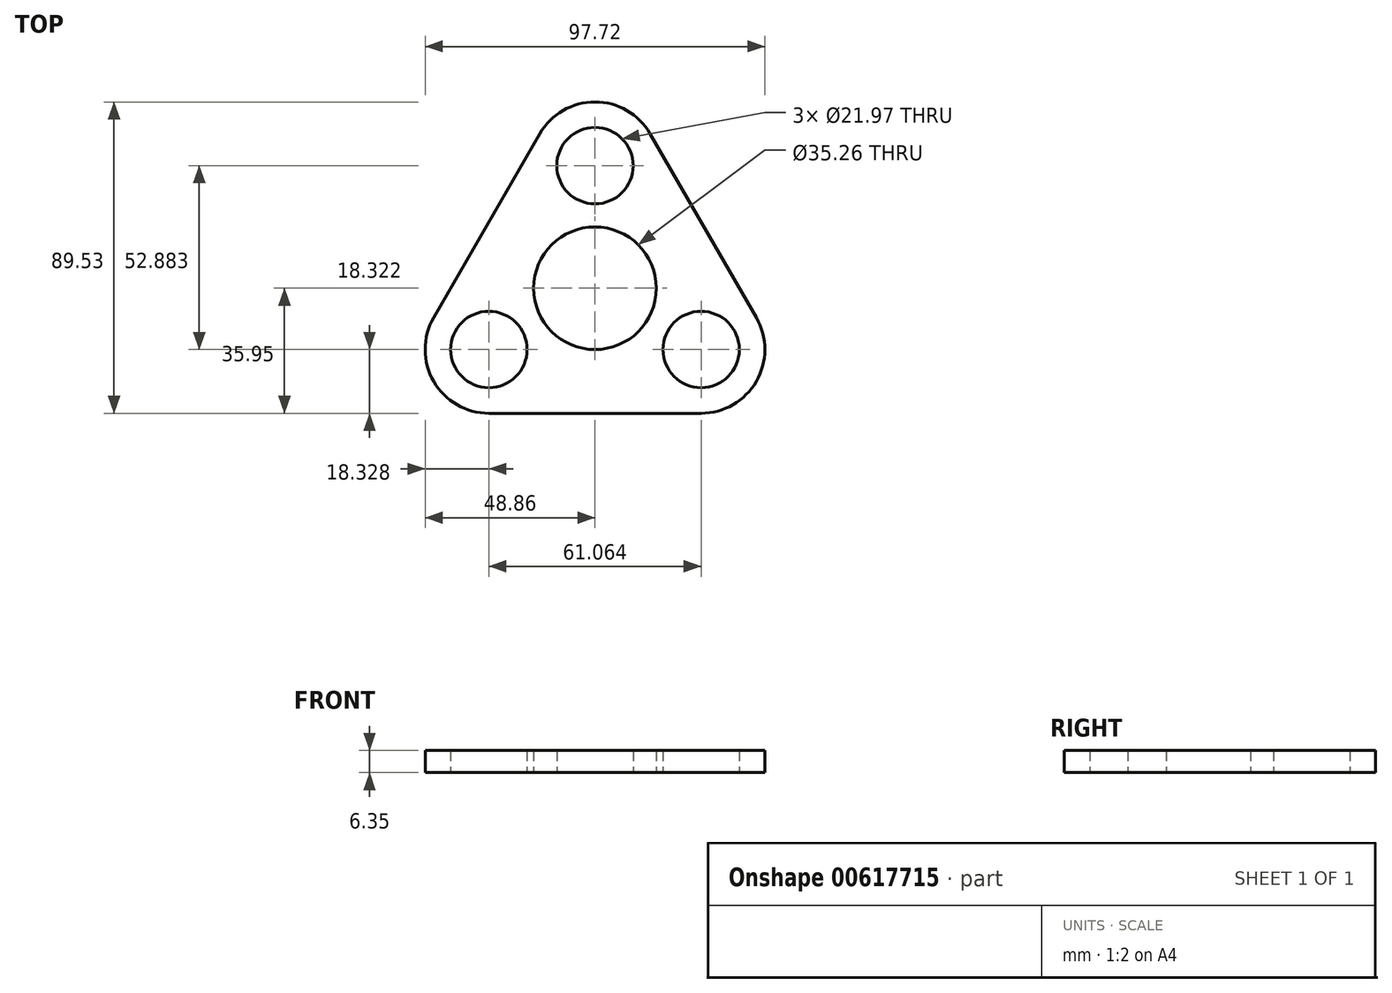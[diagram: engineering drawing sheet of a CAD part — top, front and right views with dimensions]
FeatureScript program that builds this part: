
annotation { "Feature Type Name" : "Feature", "Feature Type Description" : "" }
export const myFeature = defineFeature(function(context is Context, id is Id, definition is map)
    precondition{}
    {
        {
            var Q0;
            Q0=qCreatedBy(makeId("Top.planeOp"),FACE);
            var sketch = newSketch(context, id + "F0", { "sketchPlane" : qUnion([Q0])});
            skCircle(sketch, "E0", {"center": v(0, 0) * mm, "radius": 10.99 * mm});
            skLineSegment(sketch, "E1", {"start": v(0, 0) * mm, "end": v(0, 35.26) * mm});
            skLineSegment(sketch, "E2", {"start": v(0, 0) * mm, "end": v(30.53, -17.63) * mm});
            skLineSegment(sketch, "E3", {"start": v(0, 0) * mm, "end": v(-30.53, -17.63) * mm});
            skCircle(sketch, "E4", {"center": v(0, 35.26) * mm, "radius": 10.99 * mm});
            skCircle(sketch, "E5", {"center": v(-30.53, -17.63) * mm, "radius": 10.99 * mm});
            skCircle(sketch, "E6", {"center": v(30.53, -17.63) * mm, "radius": 10.99 * mm});
            skCircle(sketch, "E7", {"center": v(0, 0) * mm, "radius": 17.63 * mm});
            skCircle(sketch, "E8", {"center": v(-30.53, -17.63) * mm, "radius": 18.33 * mm});
            skCircle(sketch, "E9", {"center": v(0, 35.26) * mm, "radius": 18.33 * mm});
            skCircle(sketch, "E10", {"center": v(30.53, -17.63) * mm, "radius": 18.33 * mm});
            skLineSegment(sketch, "E11", {"start": v(15.87, 44.42) * mm, "end": v(46.4, -8.46) * mm});
            skLineSegment(sketch, "E12", {"start": v(-15.87, 44.42) * mm, "end": v(-46.4, -8.46) * mm});
            skLineSegment(sketch, "E13", {"start": v(-30.53, -35.95) * mm, "end": v(30.53, -35.95) * mm});
            skCircle(sketch, "E14", {"center": v(-21.16, 23.01) * mm, "radius": 6.12 * mm});
            skCircle(sketch, "E15", {"center": v(21.16, 23.01) * mm, "radius": 6.12 * mm});
            skCircle(sketch, "E16", {"center": v(0, -29.83) * mm, "radius": 6.12 * mm});
            skSolve(sketch);
        }
        {
            var Q0;
            {var subQ0=sQuery(id+"F0.wireOp",EDGE,"E12");var subQ1=sQuery(id+"F0.wireOp",EDGE,"E9");var subQ2=makeQuery(id+"F0.imprint","INTERSECT",VERTEX,{"derivedFrom":[subQ1,subQ0]});Q0=makeQuery(id+"F0.imprint","IMPRINT",FACE,{"disambiguationData":[TD([[makeQuery(id+"F0.imprint","IMPRINT",EDGE,{"disambiguationData":[TD([[subQ2,-1.0]])],"derivedFrom":subQ1}),-1.0]])]});}
            var Q1;
            {var subQ0=sQuery(id+"F0.wireOp",EDGE,"E11");var subQ1=sQuery(id+"F0.wireOp",EDGE,"E9");var subQ2=makeQuery(id+"F0.imprint","INTERSECT",VERTEX,{"derivedFrom":[subQ1,subQ0]});Q1=makeQuery(id+"F0.imprint","IMPRINT",FACE,{"disambiguationData":[TD([[makeQuery(id+"F0.imprint","IMPRINT",EDGE,{"disambiguationData":[TD([[subQ2,1.0]])],"derivedFrom":subQ1}),-1.0]])]});}
            var Q2;
            Q2 = qSketchRegion(id + "F0", true);
            extrude(context, id + "F1", {"entities" : qUnion([Q0, Q1, Q2]), "depth" : 6.35 * mm, "offsetDistance" : 25.4 * mm});
        }
    });
